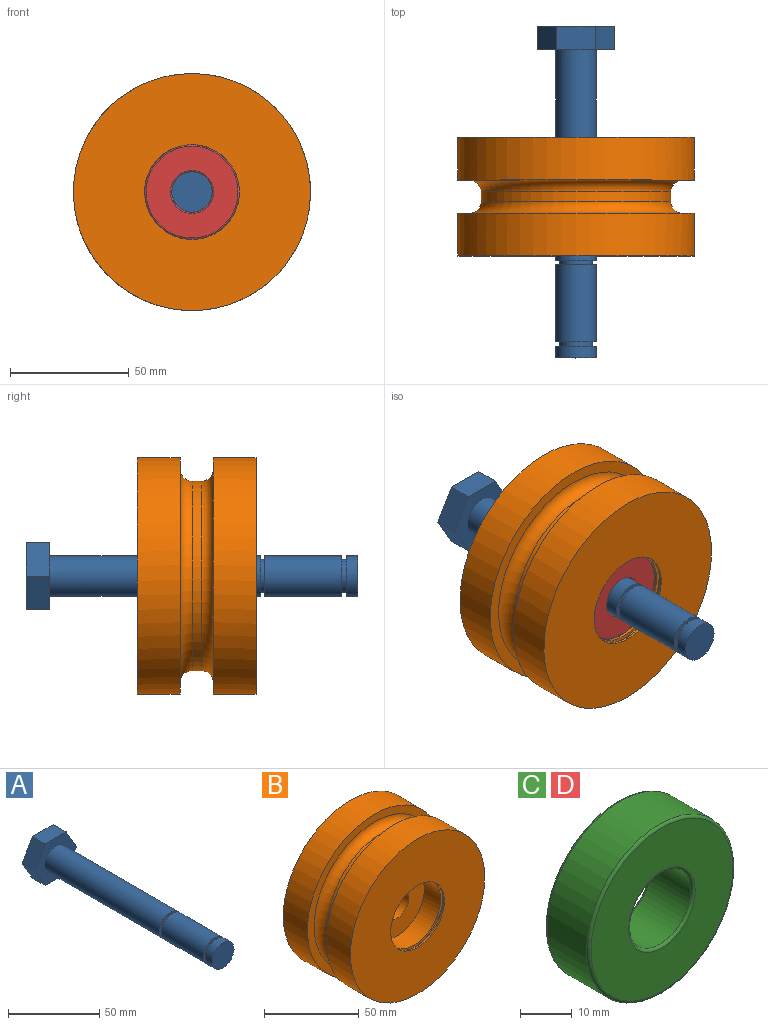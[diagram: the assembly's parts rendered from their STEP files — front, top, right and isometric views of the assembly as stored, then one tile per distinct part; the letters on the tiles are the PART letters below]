
ASSEMBLY  parts=4 mates=3
PART A: 18 faces, bbox 32.3x140x28 mm
  f0: cylinder r=8.5mm len=89mm, axis (0,1,0), area 4753.2mm2, adj f8,f10
  f1: plane 14x10mm, normal (-0.87,0,-0.5), area 161.7mm2, adj f2,f6,f7,f8
  f2: plane 14x10mm, normal (-0.87,0,0.5), area 161.7mm2, adj f1,f3,f7,f8
  f3: plane 16.17x10mm, normal (0,0,1), area 161.7mm2, adj f2,f4,f7,f8
  f4: plane 14x10mm, normal (0.87,0,0.5), area 161.7mm2, adj f3,f5,f7,f8
  f5: plane 14x10mm, normal (0.87,0,-0.5), area 161.7mm2, adj f4,f6,f7,f8
  f6: plane 16.17x10mm, normal (0,0,-1), area 161.7mm2, adj f1,f5,f7,f8
  f7: plane 32.33x28mm, normal (0,1,0), area 679mm2, adj f1,f2,f3,f4,f5,f6
  f8: plane 32.33x28mm, normal (0,-1,0), area 452mm2, adj f0,f1,f2,f3,f4,f5,f6
  f9: plane 17x17mm, normal (0,1,0), area 73mm2, adj f11,f12
  f10: plane 17x17mm, normal (0,-1,0), area 73mm2, adj f0,f11
  f11: cylinder r=7mm len=14mm, axis (0,-1,0), area 77mm2, adj f9,f10
  f12: cylinder r=8.5mm len=32.5mm, axis (0,1,0), area 1735.7mm2, adj f9,f14
  f13: plane 17x17mm, normal (0,1,0), area 73mm2, adj f15,f17
  f14: plane 17x17mm, normal (0,-1,0), area 73mm2, adj f12,f15
  f15: cylinder r=7mm len=14mm, axis (0,-1,0), area 77mm2, adj f13,f14
  f16: plane 17x17mm, normal (0,-1,0), area 227mm2, adj f17
  f17: cylinder r=8.5mm len=17mm, axis (0,1,0), area 267mm2, adj f13,f16
PART B: 22 faces, bbox 105.1x50x105.1 mm
  f0: cylinder r=20mm len=40mm, axis (0,1,0), area 125.7mm2, adj f4,f12
  f1: cylinder r=50mm len=100mm, axis (0,1,0), area 5654.9mm2, adj f3,f5
  f2: cylinder r=50mm len=100mm, axis (0,1,0), area 5654.9mm2, adj f4,f6
  f3: plane 100x100mm, normal (0,-1,0), area 6597.3mm2, adj f1,f10
  f4: plane 100x100mm, normal (0,1,0), area 6597.3mm2, adj f0,f2
  f5: plane 100x100mm, normal (0,1,0), area 1492.3mm2, adj f1,f7
  f6: plane 100x100mm, normal (0,-1,0), area 1492.3mm2, adj f2,f9
  f7: torus R=45mm, axis (0,1,0), area 2063.6mm2, adj f5,f8
  f8: cylinder r=40mm len=80mm, axis (0,1,0), area 1005.3mm2, adj f7,f9
  f9: torus R=45mm, axis (0,1,0), area 2063.6mm2, adj f6,f8
  f10: cylinder r=20mm len=40mm, axis (0,-1,0), area 125.7mm2, adj f3,f19
  f11: plane 43x43mm, normal (0,1,0), area 195.6mm2, adj f13,f18
  f12: plane 43x43mm, normal (0,-1,0), area 195.6mm2, adj f0,f13
  f13: cylinder r=21.5mm len=43mm, axis (0,-1,0), area 236.4mm2, adj f11,f12
  f14: plane 40x40mm, normal (0,-1,0), area 1029.7mm2, adj f15,f16
  f15: cylinder r=20mm len=40mm, axis (0,-1,0), area 1539.4mm2, adj f14,f20
  f16: cylinder r=8.5mm len=20mm, axis (0,1,0), area 1068.1mm2, adj f14,f17
  f17: plane 40x40mm, normal (0,1,0), area 1029.7mm2, adj f16,f18
  f18: cylinder r=20mm len=40mm, axis (0,1,0), area 1539.4mm2, adj f11,f17
  f19: plane 43x43mm, normal (0,1,0), area 195.6mm2, adj f10,f21
  f20: plane 43x43mm, normal (0,-1,0), area 195.6mm2, adj f15,f21
  f21: cylinder r=21.5mm len=43mm, axis (0,-1,0), area 236.4mm2, adj f19,f20
PART C: 8 faces, bbox 43.3x12x43.3 mm
  f0: cylinder r=8.5mm len=17mm, axis (0,1,0), area 576.8mm2, adj f4,f6
  f1: cylinder r=20mm len=40mm, axis (0,1,0), area 1357.2mm2, adj f5,f7
  f2: plane 38.8x38.8mm, normal (0,-1,0), area 922.2mm2, adj f6,f7
  f3: plane 38.8x38.8mm, normal (0,1,0), area 922.2mm2, adj f4,f5
  f4: torus R=9.1mm, axis (0,-1,0), area 51.6mm2, adj f0,f3
  f5: torus R=19.4mm, axis (0,-1,0), area 117.1mm2, adj f1,f3
  f6: torus R=9.1mm, axis (0,-1,0), area 51.6mm2, adj f0,f2
  f7: torus R=19.4mm, axis (0,-1,0), area 117.1mm2, adj f1,f2
PART D: same geometry as C
PLACE A t=(1.75,60.72,0.73)mm
PLACE B t=(1.75,-1.28,0.73)mm
PLACE C t=(1.75,14.12,0.73)mm
PLACE D rot(axis=(1,0,0),180deg) t=(1.75,-16.68,0.73)mm
MATE fastened C.f0 <-> B.f0  axis (0,1,0) through (1.75,8.72,0.73)mm
MATE fastened D.f0 <-> B.f0  axis (0,-1,0) through (1.75,-11.28,0.73)mm
MATE fastened A.f0 <-> B.f0  axis (0,-1,0) through (1.75,-69.28,0.73)mm
